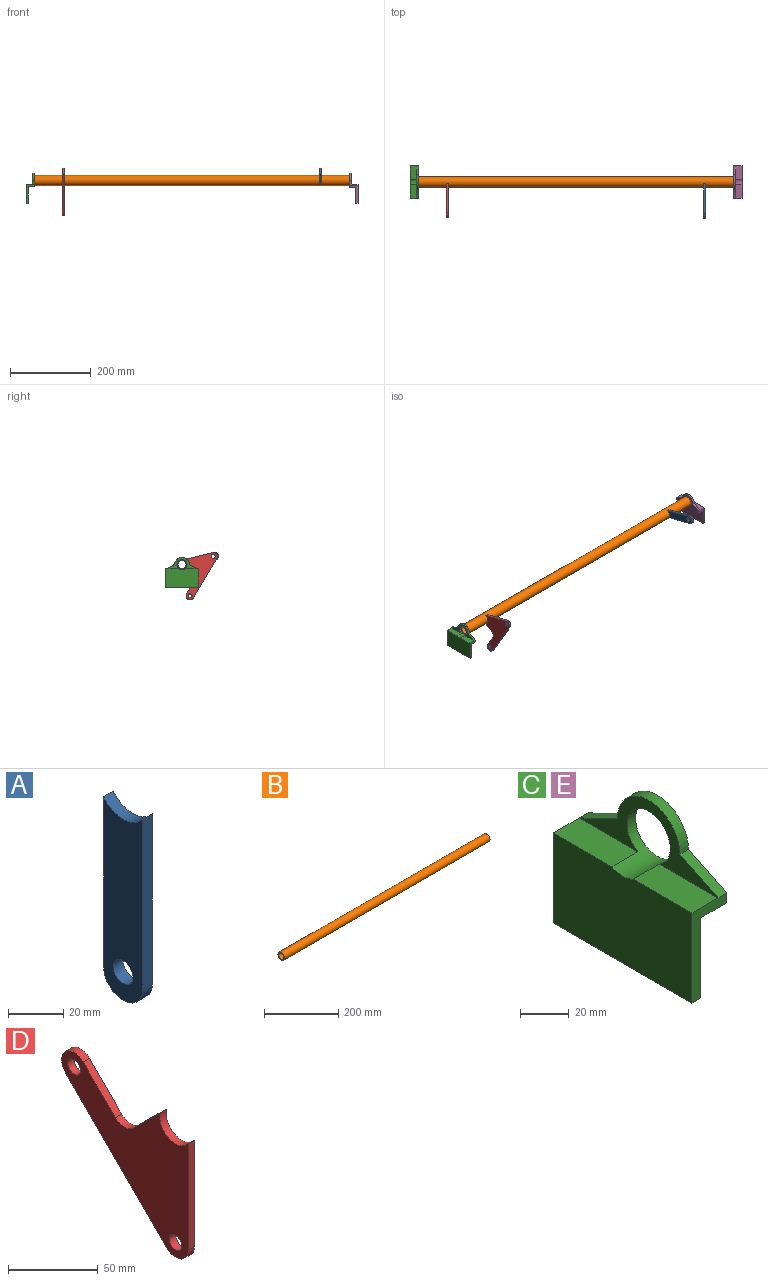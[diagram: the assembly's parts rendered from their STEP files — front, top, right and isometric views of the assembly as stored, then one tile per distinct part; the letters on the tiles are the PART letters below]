
ASSEMBLY  parts=5 mates=4
PART A: 7 faces, bbox 5x20x85 mm
  f0: cylinder r=12.5mm len=20mm, axis (-1,0,0), area 115.9mm2, adj f1,f3,f5,f6
  f1: plane 75x5mm, normal (0,-1,0), area 375mm2, adj f0,f2,f5,f6
  f2: cylinder r=10mm len=20mm, axis (-1,0,0), area 157.1mm2, adj f1,f3,f5,f6
  f3: plane 75x5mm, normal (0,1,0), area 375mm2, adj f0,f2,f5,f6
  f4: cylinder r=5mm len=10mm, axis (-1,0,0), area 157.1mm2, adj f5,f6
  f5: plane 85x20mm, normal (1,0,0), area 1508.6mm2, adj f0,f1,f2,f3,f4
  f6: plane 85x20mm, normal (-1,0,0), area 1508.6mm2, adj f0,f1,f2,f3,f4
PART B: 4 faces, bbox 780x25x25 mm
  f0: cylinder r=10mm len=780mm, axis (-1,0,0), area 49008.8mm2, adj f2,f3
  f1: cylinder r=12.5mm len=780mm, axis (-1,0,0), area 61261.1mm2, adj f2,f3
  f2: plane 25x25mm, normal (1,0,0), area 176.7mm2, adj f0,f1
  f3: plane 25x25mm, normal (-1,0,0), area 176.7mm2, adj f0,f1
PART C: 14 faces, bbox 20x80x73.9 mm
  f0: plane 80x15mm, normal (0,0,-1), area 1200mm2, adj f6,f9,f10,f13
  f1: cylinder r=12.5mm len=25mm, axis (1,0,0), area 586.9mm2, adj f5,f6,f7,f8,f11
  f2: plane 22x10.86mm, normal (0,0.44,0.9), area 122.7mm2, adj f3,f5,f6,f10
  f3: cylinder r=18mm len=36mm, axis (1,0,0), area 282.7mm2, adj f2,f4,f5,f6
  f4: plane 22x10.86mm, normal (0,-0.44,0.9), area 122.7mm2, adj f3,f5,f6,f9
  f5: plane 80x28.86mm, normal (-1,0,0), area 661.7mm2, adj f1,f2,f3,f4,f7,f8
  f6: plane 80x33.86mm, normal (1,0,0), area 1048mm2, adj f0,f1,f2,f3,f4,f9,f10
  f7: plane 33.81x15mm, normal (0,0,1), area 507.2mm2, adj f1,f5,f10,f11
  f8: plane 33.81x15mm, normal (0,0,1), area 507.2mm2, adj f1,f5,f9,f11
  f9: plane 45x20mm, normal (0,-1,0), area 300mm2, adj f0,f4,f6,f8,f11,f12,f13
  f10: plane 45x20mm, normal (0,1,0), area 300mm2, adj f0,f2,f6,f7,f11,f12,f13
  f11: plane 80x45mm, normal (-1,0,0), area 3586.3mm2, adj f1,f7,f8,f9,f10,f12
  f12: plane 80x5mm, normal (0,0,-1), area 400mm2, adj f9,f10,f11,f13
  f13: plane 80x40mm, normal (1,0,0), area 3200mm2, adj f0,f9,f10,f12
PART D: 12 faces, bbox 5x100x100 mm
  f0: cylinder r=12.5mm len=22.5mm, axis (-1,0,0), area 169.4mm2, adj f1,f8,f10,f11
  f1: plane 72.5x5mm, normal (0,-1,0), area 362.5mm2, adj f0,f2,f10,f11
  f2: cylinder r=10mm len=17.07mm, axis (-1,0,0), area 117.8mm2, adj f1,f3,f10,f11
  f3: plane 80x80mm, normal (0,0.71,-0.71), area 565.7mm2, adj f2,f4,f10,f11
  f4: cylinder r=10mm len=17.07mm, axis (-1,0,0), area 157.1mm2, adj f3,f5,f10,f11
  f5: plane 25.5x25.5mm, normal (0,-0.71,0.71), area 180.3mm2, adj f4,f6,f10,f11
  f6: cylinder r=10mm len=14.14mm, axis (-1,0,0), area 78.5mm2, adj f5,f8,f10,f11
  f7: cylinder r=5mm len=10mm, axis (-1,0,0), area 157.1mm2, adj f10,f11
  f8: plane 21.07x21.07mm, normal (0,0.71,0.71), area 149mm2, adj f0,f6,f10,f11
  f9: cylinder r=5mm len=10mm, axis (-1,0,0), area 157.1mm2, adj f10,f11
  f10: plane 100x100mm, normal (1,0,0), area 4440.6mm2, adj f0,f1,f2,f3,f4,f5,f6,f7
  f11: plane 100x100mm, normal (-1,0,0), area 4440.6mm2, adj f0,f1,f2,f3,f4,f5,f6,f7
PART E: same geometry as C
PLACE A rot(axis=(-1,0,0),104.4deg) t=(725,-49.2,-380.06)mm
PLACE B rot(axis=(-1,0,0),104.4deg) t=(20,187.98,-145.2)mm
PLACE C t=(20,187.98,-145.2)mm
PLACE D rot(axis=(-1,0,0),104.4deg) t=(90,219.53,-320.23)mm
PLACE E rot(axis=(0,0,1),180deg) t=(800,187.98,-145.2)mm
MATE revolute E.f1 <-> B.f1  axis (-1,0,0) through (800,187.98,-145.2)mm
MATE fastened B.f1 <-> A.f0  axis (1,0,0) through (800,187.98,-145.2)mm
MATE fastened B.f1 <-> D.f0  axis (1,0,0) through (800,187.98,-145.2)mm
MATE revolute B.f1 <-> C.f1  axis (-1,0,0) through (20,187.98,-145.2)mm
